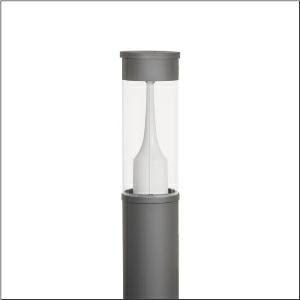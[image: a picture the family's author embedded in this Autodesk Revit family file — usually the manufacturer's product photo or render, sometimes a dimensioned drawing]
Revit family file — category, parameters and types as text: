
# Revit family: city-light_260_iq___st1_2a_5xa5295ef14h_2f06
name_source: partatom
category: Lighting Fixtures
units: mm (PartAtom-declared; Revit-internal decimal feet)

## family parameters
Cut with Voids When Loaded = No
Host = Face
Light Source = No
Part Type = Normal
Room Calculation Point = No
Round Connector Dimension = Use Diameter
Shared = No

## types (1)
- --- (1 x LED, 1540 lm, 10.5 W, 3000K)
    Apparent Load = 11 VA
    CIE Flux Codes = 22 61 93 96 100
    Color Rendering = 70
    Color Temperature = 3000K
    Default Elevation = 1800 mm
    Description = City-Light 260 iQ, light pillar, Module 540 iQ-SR, primary light control with 3 zone facetted reflector, of plastic, silver coated, highly specular, structured, primary optical cover: cover, of PMMA, transparent, light distribution: ST1.2a, primary light characteristic: asymmetric, LED, High Power LED, rated luminous flux: 1.540lm, luminous efficacy: 147lm/W, light colour: 730, colour temperature: 3000K, control gear: ECG iQ, control: Auto-Match, Temp-Guard, Lumen-Switch, Night-Set, Smart-Wire, Light-Fading, Desk-Remote (wireless, voltage-free reading and setting of iQ features in the workshop via application-optimized NFC function/RFID function), optimised constant luminous flux control (CLO 2.0), Street-Remote, presetting dimming logarithmic, with terminal, 6-pole, max. 2.5mm², mains connection: 230..240V, AC, 50/60Hz, start of lifetime: 11W, end of service life: 11W, reduction: 5W, luminaire housing, cylindrical, of extruded aluminium section, coated, Siteco® metallic grey (DB 702S), length: 2.600mm, diameter: 200mm, Module 540 iQ-SR, traffic white (RAL 9016), equipment: standard, protection rating (complete): IP65, insulation class (complete): insulation class II (safety insulation), certification: CE, ENEC, VDE, packaging unit: 1 piece

Light Distribution: ST1.2a
    Height = 500 mm
    Lamp = 1 x LED
    Lamp Light Flux = 1540 lm
    Lamp Power = 10.5 W
    Lamp count = 1
    Length = 200 mm  [stored 0.656168 ft]
    Luminous efficacy = 147 lm/W
    Manufacturer = Siteco
    ModVariant = No
    Model = 5XA5295EF14H
    Mounting Place = Floor
    Mounting Type = Freestanding
    Number of Poles = 1
    OnlyDefault = Yes
    Power Factor = 1
    Product Name = City-Light 260 iQ | ST1.2a
    Product group = light pillar
    ProductGroupID = 1303
    Protection Class = Protection class II
    Protection Degree = IP 65
    RLX_Detail_Level = 1
    RLX_Emergency_Light_Flux = 0 lm
    RLX_Emergency_Type = 0
    RLX_Emergency_Type_DB = No
    RlxData = <blob elided: 60429 chars, md5=1c1095d0>
    Socket = socket
    Standby Power = 0 W
    System Light Flux = 1540 lm
    System Power = 11 W
    Type Comments = factory setting: luminous flux: 100 % | dim-lin: 254 | 419 mA
    Type Image = l_1006918.jpg
    URL = http://relux.com
    VarID = @adj_091527
    Voltage = 0 V
    Weight = 0.00 kg
    Width = 0 mm  [stored 0 ft]

note: [stored X ft] marks values corroborated as IEEE doubles in the binary element streams (Revit-internal decimal feet)

## geometry (parser evidence)
native form markers: Blend x4, Sweep x10
no freeform markers — native parametric forms only
